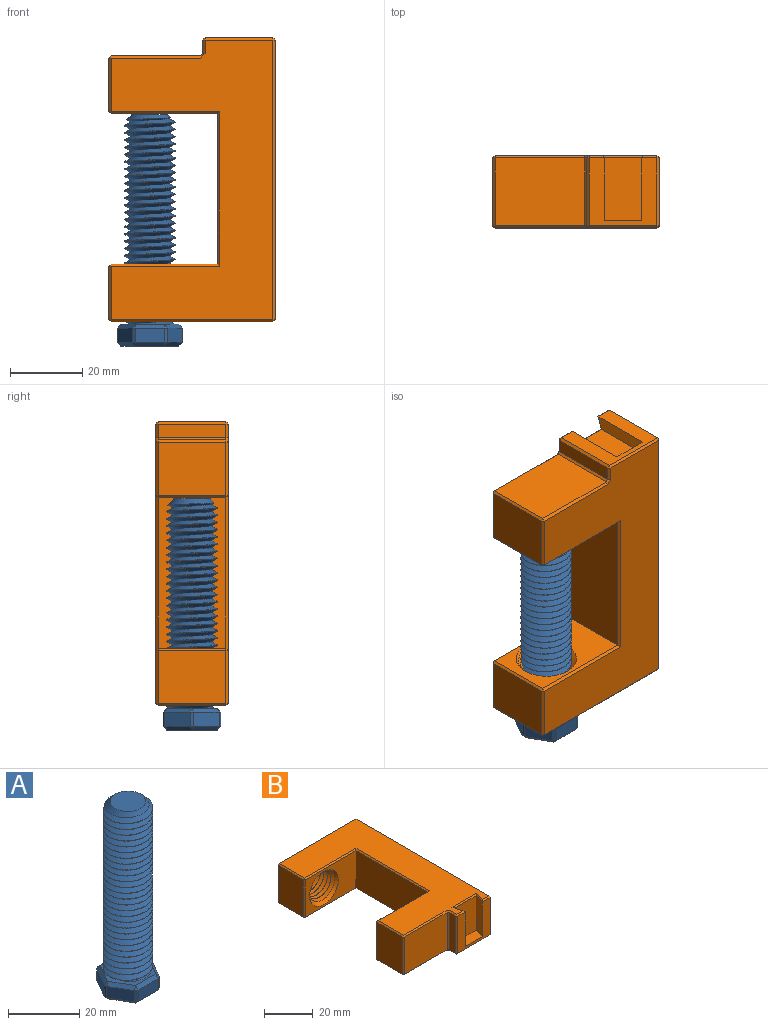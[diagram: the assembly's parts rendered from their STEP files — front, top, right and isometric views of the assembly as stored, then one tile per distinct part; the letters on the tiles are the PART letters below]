
ASSEMBLY  parts=2 mates=1
PART A: 44 faces, bbox 19.2x17.5x65.9 mm
  f0: cylinder r=7mm len=56mm, axis (0,0,-1), area 524.6mm2, adj f2,f4,f5,f13
  f1: plane 10x10mm, normal (0,0,1), area 78.5mm2, adj f3
  f2: cone r=5mm half-angle=45deg, axis (0,0,-1), area 13mm2, adj f0,f3,f4,f5
  f3: cone r=5mm half-angle=45deg, axis (0,0,-1), area 48.9mm2, adj f1,f2,f5
  f4: bspline ~58.95x16.17mm, area 2105.2mm2, adj f0,f2,f5,f13
  f5: bspline ~59.62x16.17mm, area 2096.3mm2, adj f0,f2,f3,f4,f13
  f6: plane 8.04x3.92mm, normal (0,1,0), area 31.5mm2, adj f20,f21,f29,f30
  f7: plane 6.96x4.02mm, normal (-0.87,0.5,0), area 31.5mm2, adj f30,f31,f39,f40
  f8: plane 6.96x4.02mm, normal (-0.87,-0.5,0), area 31.5mm2, adj f32,f37,f40,f43
  f9: plane 8.04x3.92mm, normal (0,-1,0), area 31.5mm2, adj f26,f27,f37,f38
  f10: plane 6.96x4.02mm, normal (0.87,-0.5,0), area 31.5mm2, adj f17,f18,f27,f28
  f11: plane 6.96x4.02mm, normal (0.87,0.5,0), area 31.5mm2, adj f14,f18,f19,f20
  f12: plane 16.08x13.92mm, normal (0,0,-1), area 167.8mm2, adj f19,f28,f29,f38,f39,f43
  f13: plane 17.38x15.22mm, normal (0,0,1), area 45.6mm2, adj f0,f4,f5,f14,f17,f21,f26,f31
  f14: plane 7.48x4.92mm, normal (0.61,0.35,0.71), area 11.8mm2, adj f11,f13,f15,f16
  f15: plane 1.04x1.04mm, normal (0.76,0,0.65), area 0.7mm2, adj f14,f17,f18
  f16: plane 1.04x1.04mm, normal (0.38,0.65,0.65), area 0.7mm2, adj f14,f20,f21
  f17: plane 7.48x4.92mm, normal (0.61,-0.35,0.71), area 11.8mm2, adj f10,f13,f15,f22
  f18: plane 3.92x1.04mm, normal (1,0,0), area 4.1mm2, adj f10,f11,f15,f23
  f19: plane 7.48x4.92mm, normal (0.61,0.35,-0.71), area 11.8mm2, adj f11,f12,f23,f24
  f20: plane 3.92x0.9mm, normal (0.5,0.87,0), area 4.1mm2, adj f6,f11,f16,f24
  f21: plane 8.04x1.04mm, normal (0,0.71,0.71), area 11.8mm2, adj f6,f13,f16,f25
  f22: plane 1.04x1.04mm, normal (0.38,-0.65,0.65), area 0.7mm2, adj f17,f26,f27
  f23: plane 1.04x1.04mm, normal (0.76,0,-0.65), area 0.7mm2, adj f18,f19,f28
  f24: plane 1.04x1.04mm, normal (0.38,0.65,-0.65), area 0.7mm2, adj f19,f20,f29
  f25: plane 1.04x1.04mm, normal (-0.38,0.65,0.65), area 0.7mm2, adj f21,f30,f31
  f26: plane 8.04x1.04mm, normal (0,-0.71,0.71), area 11.8mm2, adj f9,f13,f22,f33
  f27: plane 3.92x0.9mm, normal (0.5,-0.87,0), area 4.1mm2, adj f9,f10,f22,f34
  f28: plane 7.48x4.92mm, normal (0.61,-0.35,-0.71), area 11.8mm2, adj f10,f12,f23,f34
  f29: plane 8.04x1.04mm, normal (0,0.71,-0.71), area 11.8mm2, adj f6,f12,f24,f35
  f30: plane 3.92x0.9mm, normal (-0.5,0.87,0), area 4.1mm2, adj f6,f7,f25,f35
  f31: plane 7.48x4.92mm, normal (-0.61,0.35,0.71), area 11.8mm2, adj f7,f13,f25,f36
  f32: plane 7.48x4.92mm, normal (-0.61,-0.35,0.71), area 11.8mm2, adj f8,f13,f33,f36
  f33: plane 1.04x1.04mm, normal (-0.38,-0.65,0.65), area 0.7mm2, adj f26,f32,f37
  f34: plane 1.04x1.04mm, normal (0.38,-0.65,-0.65), area 0.7mm2, adj f27,f28,f38
  f35: plane 1.04x1.04mm, normal (-0.38,0.65,-0.65), area 0.7mm2, adj f29,f30,f39
  f36: plane 1.04x1.04mm, normal (-0.76,0,0.65), area 0.7mm2, adj f31,f32,f40
  f37: plane 3.92x0.9mm, normal (-0.5,-0.87,0), area 4.1mm2, adj f8,f9,f33,f41
  f38: plane 8.04x1.04mm, normal (0,-0.71,-0.71), area 11.8mm2, adj f9,f12,f34,f41
  f39: plane 7.48x4.92mm, normal (-0.61,0.35,-0.71), area 11.8mm2, adj f7,f12,f35,f42
  f40: plane 3.92x1.04mm, normal (-1,0,0), area 4.1mm2, adj f7,f8,f36,f42
  f41: plane 1.04x1.04mm, normal (-0.38,-0.65,-0.65), area 0.7mm2, adj f37,f38,f43
  f42: plane 1.04x1.04mm, normal (-0.76,0,-0.65), area 0.7mm2, adj f39,f40,f43
  f43: plane 7.48x4.92mm, normal (-0.61,-0.35,-0.71), area 11.8mm2, adj f8,f12,f41,f42
PART B: 72 faces, bbox 46x79.2x20 mm
  f0: plane 29.4x18.8mm, normal (0,1,0), area 552.7mm2, adj f12,f32,f36,f37
  f1: plane 18.8x14.8mm, normal (-1,0,0), area 278.2mm2, adj f37,f42,f47,f48
  f2: plane 24.8x18.8mm, normal (0,-1,0), area 466.2mm2, adj f48,f54,f58,f59
  f3: plane 18.8x3.8mm, normal (-1,0,0), area 71.4mm2, adj f59,f64,f67,f70
  f4: plane 17.4x5mm, normal (0.97,0.26,0), area 90.1mm2, adj f5,f7,f15,f61
  f5: plane 17.4x12.68mm, normal (0,-1,0), area 220.6mm2, adj f4,f6,f15,f55
  f6: plane 17.4x5mm, normal (-0.97,0.26,0), area 90.1mm2, adj f5,f7,f15,f50
  f7: plane 18.8x18.8mm, normal (0,-1,0), area 179.4mm2, adj f4,f6,f15,f43,f56,f65,f66,f70
  f8: plane 77.4x18.8mm, normal (1,0,0), area 1455.1mm2, adj f44,f45,f56,f57
  f9: plane 44.8x18.8mm, normal (0,1,0), area 610mm2, adj f33,f34,f45,f46,f71
  f10: plane 18.8x14.8mm, normal (-1,0,0), area 278.2mm2, adj f25,f26,f34,f35
  f11: plane 29.4x18.8mm, normal (0,-1,0), area 333.7mm2, adj f12,f20,f24,f26,f27
  f12: plane 41.6x18.8mm, normal (-1,0,0), area 782.1mm2, adj f0,f11,f28,f31
  f13: plane 77.4x44.8mm, normal (0,0,1), area 1989.7mm2, adj f24,f25,f28,f32,f33,f42,f43,f44
  f14: plane 77.4x44.8mm, normal (0,0,-1), area 2054.2mm2, adj f27,f31,f35,f36,f46,f47,f57,f58
  f15: plane 12.68x5mm, normal (0,0,1), area 56.7mm2, adj f4,f5,f6,f7
  f16: cylinder r=6.35mm len=12.7mm, axis (0,-1,0), area 22.5mm2, adj f17,f18,f19,f21,f22
  f17: cone r=8.35mm half-angle=45deg, axis (0,1,0), area 69.7mm2, adj f16,f18,f21,f22,f71
  f18: cone r=8.35mm half-angle=45deg, axis (0,1,0), area 0.1mm2, adj f16,f17,f22
  f19: cone r=6.35mm half-angle=45deg, axis (0,-1,0), area 14.4mm2, adj f16,f20,f21,f22
  f20: cone r=6.35mm half-angle=45deg, axis (0,-1,0), area 68.5mm2, adj f11,f19,f22
  f21: bspline ~18.46x16.28mm, area 583.9mm2, adj f16,f17,f19,f22
  f22: bspline ~18.46x16.28mm, area 586.9mm2, adj f16,f17,f18,f19,f20,f21
  f23: plane 0.6x0.6mm, normal (-0.58,-0.58,0.58), area 0.3mm2, adj f24,f25,f26
  f24: plane 30x0.6mm, normal (0,-0.71,0.71), area 25.2mm2, adj f11,f13,f23,f28
  f25: plane 14.8x0.6mm, normal (-0.71,0,0.71), area 12.6mm2, adj f10,f13,f23,f29
  f26: plane 18.8x0.6mm, normal (-0.71,-0.71,0), area 16mm2, adj f10,f11,f23,f30
  f27: plane 30x0.6mm, normal (0,-0.71,-0.71), area 25.2mm2, adj f11,f14,f30,f31
  f28: plane 42.8x0.6mm, normal (-0.71,0,0.71), area 35.8mm2, adj f12,f13,f24,f32
  f29: plane 0.6x0.6mm, normal (-0.58,0.58,0.58), area 0.3mm2, adj f25,f33,f34
  f30: plane 0.6x0.6mm, normal (-0.58,-0.58,-0.58), area 0.3mm2, adj f26,f27,f35
  f31: plane 42.8x0.6mm, normal (-0.71,0,-0.71), area 35.8mm2, adj f12,f14,f27,f36
  f32: plane 30x0.6mm, normal (0,0.71,0.71), area 25.2mm2, adj f0,f13,f28,f38
  f33: plane 44.8x0.6mm, normal (0,0.71,0.71), area 38mm2, adj f9,f13,f29,f39
  f34: plane 18.8x0.6mm, normal (-0.71,0.71,0), area 16mm2, adj f9,f10,f29,f40
  f35: plane 14.8x0.6mm, normal (-0.71,0,-0.71), area 12.6mm2, adj f10,f14,f30,f40
  f36: plane 30x0.6mm, normal (0,0.71,-0.71), area 25.2mm2, adj f0,f14,f31,f41
  f37: plane 18.8x0.6mm, normal (-0.71,0.71,0), area 16mm2, adj f0,f1,f38,f41
  f38: plane 0.6x0.6mm, normal (-0.58,0.58,0.58), area 0.3mm2, adj f32,f37,f42
  f39: plane 0.6x0.6mm, normal (0.58,0.58,0.58), area 0.3mm2, adj f33,f44,f45
  f40: plane 0.6x0.6mm, normal (-0.58,0.58,-0.58), area 0.3mm2, adj f34,f35,f46
  f41: plane 0.6x0.6mm, normal (-0.58,0.58,-0.58), area 0.3mm2, adj f36,f37,f47
  f42: plane 14.8x0.6mm, normal (-0.71,0,0.71), area 12.6mm2, adj f1,f13,f38,f49
  f43: plane 4.4x0.6mm, normal (0,-0.71,0.71), area 3.4mm2, adj f7,f13,f50,f51
  f44: plane 77.4x0.6mm, normal (0.71,0,0.71), area 65.7mm2, adj f8,f13,f39,f51
  f45: plane 18.8x0.6mm, normal (0.71,0.71,0), area 16mm2, adj f8,f9,f39,f52
  f46: plane 44.8x0.6mm, normal (0,0.71,-0.71), area 38mm2, adj f9,f14,f40,f52
  f47: plane 14.8x0.6mm, normal (-0.71,0,-0.71), area 12.6mm2, adj f1,f14,f41,f53
  f48: plane 18.8x0.6mm, normal (-0.71,-0.71,0), area 16mm2, adj f1,f2,f49,f53
  f49: plane 0.6x0.6mm, normal (-0.58,-0.58,0.58), area 0.3mm2, adj f42,f48,f54
  f50: plane 5.6x2.12mm, normal (-0.68,0.18,0.71), area 4.4mm2, adj f6,f13,f43,f55
  f51: plane 0.6x0.6mm, normal (0.58,-0.58,0.58), area 0.3mm2, adj f43,f44,f56
  f52: plane 0.6x0.6mm, normal (0.58,0.58,-0.58), area 0.3mm2, adj f45,f46,f57
  f53: plane 0.6x0.6mm, normal (-0.58,-0.58,-0.58), area 0.3mm2, adj f47,f48,f58
  f54: plane 24.8x0.6mm, normal (0,-0.71,0.71), area 21mm2, adj f2,f13,f49,f60
  f55: plane 14.24x0.6mm, normal (0,-0.71,0.71), area 11.4mm2, adj f5,f13,f50,f61
  f56: plane 18.8x0.6mm, normal (0.71,-0.71,0), area 16mm2, adj f7,f8,f51,f62
  f57: plane 77.4x0.6mm, normal (0.71,0,-0.71), area 65.7mm2, adj f8,f14,f52,f62
  f58: plane 24.8x0.6mm, normal (0,-0.71,-0.71), area 21mm2, adj f2,f14,f53,f63
  f59: plane 18.8x0.6mm, normal (-0.71,-0.71,0), area 16mm2, adj f2,f3,f60,f63
  f60: plane 1.2x1.2mm, normal (-0.58,-0.58,0.58), area 0.9mm2, adj f13,f54,f59,f64
  f61: plane 5.6x2.12mm, normal (0.68,0.18,0.71), area 4.4mm2, adj f4,f13,f55,f65
  f62: plane 0.6x0.6mm, normal (0.58,-0.58,-0.58), area 0.3mm2, adj f56,f57,f66
  f63: plane 1.2x1.2mm, normal (-0.58,-0.58,-0.58), area 0.9mm2, adj f14,f58,f59,f67
  f64: plane 3.8x0.6mm, normal (-0.71,0,0.71), area 3.2mm2, adj f3,f13,f60,f68
  f65: plane 4.4x0.6mm, normal (0,-0.71,0.71), area 3.4mm2, adj f7,f13,f61,f68
  f66: plane 18.8x0.6mm, normal (0,-0.71,-0.71), area 16mm2, adj f7,f14,f62,f69
  f67: plane 3.8x0.6mm, normal (-0.71,0,-0.71), area 3.2mm2, adj f3,f14,f63,f69
  f68: plane 0.6x0.6mm, normal (-0.58,-0.58,0.58), area 0.3mm2, adj f64,f65,f70
  f69: plane 0.6x0.6mm, normal (-0.58,-0.58,-0.58), area 0.3mm2, adj f66,f67,f70
  f70: plane 18.8x0.6mm, normal (-0.71,-0.71,0), area 16mm2, adj f3,f7,f68,f69
  f71: cone r=8.6mm half-angle=67.5deg, axis (0,1,0), area 24.2mm2, adj f9,f17
PLACE A t=(8.11,20.25,31.86)mm
PLACE B rot(axis=(-1,0,0),90deg) t=(-3.24,10.25,108.17)mm
MATE cylindrical B.f16 <-> A.f0  axis (0,0,1) through (8.11,20.25,50.57)mm
